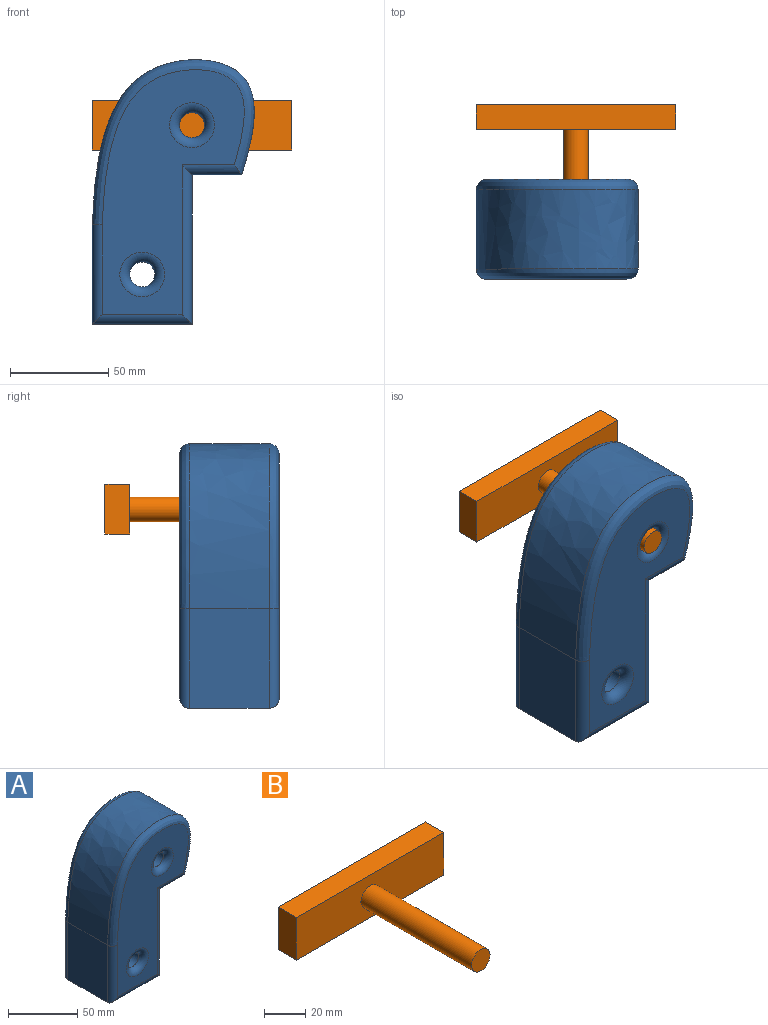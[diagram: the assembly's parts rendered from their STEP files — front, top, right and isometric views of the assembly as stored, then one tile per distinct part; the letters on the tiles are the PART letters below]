
ASSEMBLY  parts=2 mates=1
PART A: 23 faces, bbox 82.6x50.8x135 mm
  f0: plane 50.8x40.64mm, normal (0,0,-1), area 2064.5mm2, adj f1,f5,f12,f19
  f1: plane 76.2x40.64mm, normal (1,0,0), area 3096.8mm2, adj f0,f2,f10,f17
  f2: plane 40.64x25.4mm, normal (0,0,-1), area 1032.3mm2, adj f1,f3,f11,f18
  f3: extruded ~84.14x82.48mm, area 7740.4mm2, adj f2,f5,f13,f20
  f4: cylinder r=6.35mm len=40.64mm, axis (0,1,0), area 1621.5mm2, adj f9,f16
  f5: plane 50.8x40.64mm, normal (-1,0,0), area 2064.5mm2, adj f0,f3,f14,f21
  f6: cylinder r=6.35mm len=40.64mm, axis (0,1,0), area 1621.5mm2, adj f15,f22
  f7: plane 124.81x72.41mm, normal (0,-1,0), area 5010.6mm2, adj f9,f10,f11,f12,f13,f14,f15
  f8: plane 124.81x72.42mm, normal (0,1,0), area 5010.6mm2, adj f16,f17,f18,f19,f20,f21,f22
  f9: torus R=11.43mm, axis (0,-1,0), area 410.9mm2, adj f4,f7
  f10: cylinder r=5.08mm len=81.28mm, axis (0,0,-1), area 608mm2, adj f1,f7,f11,f12
  f11: cylinder r=5.08mm len=30.48mm, axis (-1,0,0), area 208mm2, adj f2,f7,f10,f13
  f12: cylinder r=5.08mm len=50.8mm, axis (-1,0,0), area 364.8mm2, adj f0,f7,f10,f14
  f13: bspline ~86.04x82.59mm, area 1454.4mm2, adj f3,f7,f11,f14
  f14: cylinder r=5.08mm len=50.8mm, axis (0,0,1), area 384.8mm2, adj f5,f7,f12,f13
  f15: torus R=11.43mm, axis (0,-1,0), area 410.9mm2, adj f6,f7
  f16: torus R=11.43mm, axis (0,-1,0), area 410.9mm2, adj f4,f8
  f17: cylinder r=5.08mm len=81.28mm, axis (0,0,1), area 608mm2, adj f1,f8,f18,f19
  f18: cylinder r=5.08mm len=30.48mm, axis (1,0,0), area 208mm2, adj f2,f8,f17,f20
  f19: cylinder r=5.08mm len=50.8mm, axis (1,0,0), area 364.8mm2, adj f0,f8,f17,f21
  f20: bspline ~86.04x82.6mm, area 1454.4mm2, adj f3,f8,f18,f21
  f21: cylinder r=5.08mm len=50.8mm, axis (0,0,-1), area 384.8mm2, adj f5,f8,f19,f20
  f22: torus R=11.43mm, axis (0,-1,0), area 410.9mm2, adj f6,f8
PART B: 8 faces, bbox 101.6x88.9x25.4 mm
  f0: plane 101.6x12.7mm, normal (0,0,-1), area 1290.3mm2, adj f1,f3,f4,f5
  f1: plane 25.4x12.7mm, normal (1,0,0), area 322.6mm2, adj f0,f2,f4,f5
  f2: plane 101.6x12.7mm, normal (0,0,1), area 1290.3mm2, adj f1,f3,f4,f5
  f3: plane 25.4x12.7mm, normal (-1,0,0), area 322.6mm2, adj f0,f2,f4,f5
  f4: plane 101.6x25.4mm, normal (0,-1,0), area 2454mm2, adj f0,f1,f2,f3,f6
  f5: plane 101.6x25.4mm, normal (0,1,0), area 2580.6mm2, adj f0,f1,f2,f3
  f6: cylinder r=6.35mm len=76.2mm, axis (0,1,0), area 3040.2mm2, adj f4,f7
  f7: plane 12.7x12.7mm, normal (0,-1,0), area 126.7mm2, adj f6
PLACE A t=(-40.82,4.42,-24.7)mm
PLACE B t=(-15.42,42.52,51.5)mm
MATE slider B.f6 <-> A.f4  axis (0,-1,0) through (-15.42,-46.38,51.5)mm
